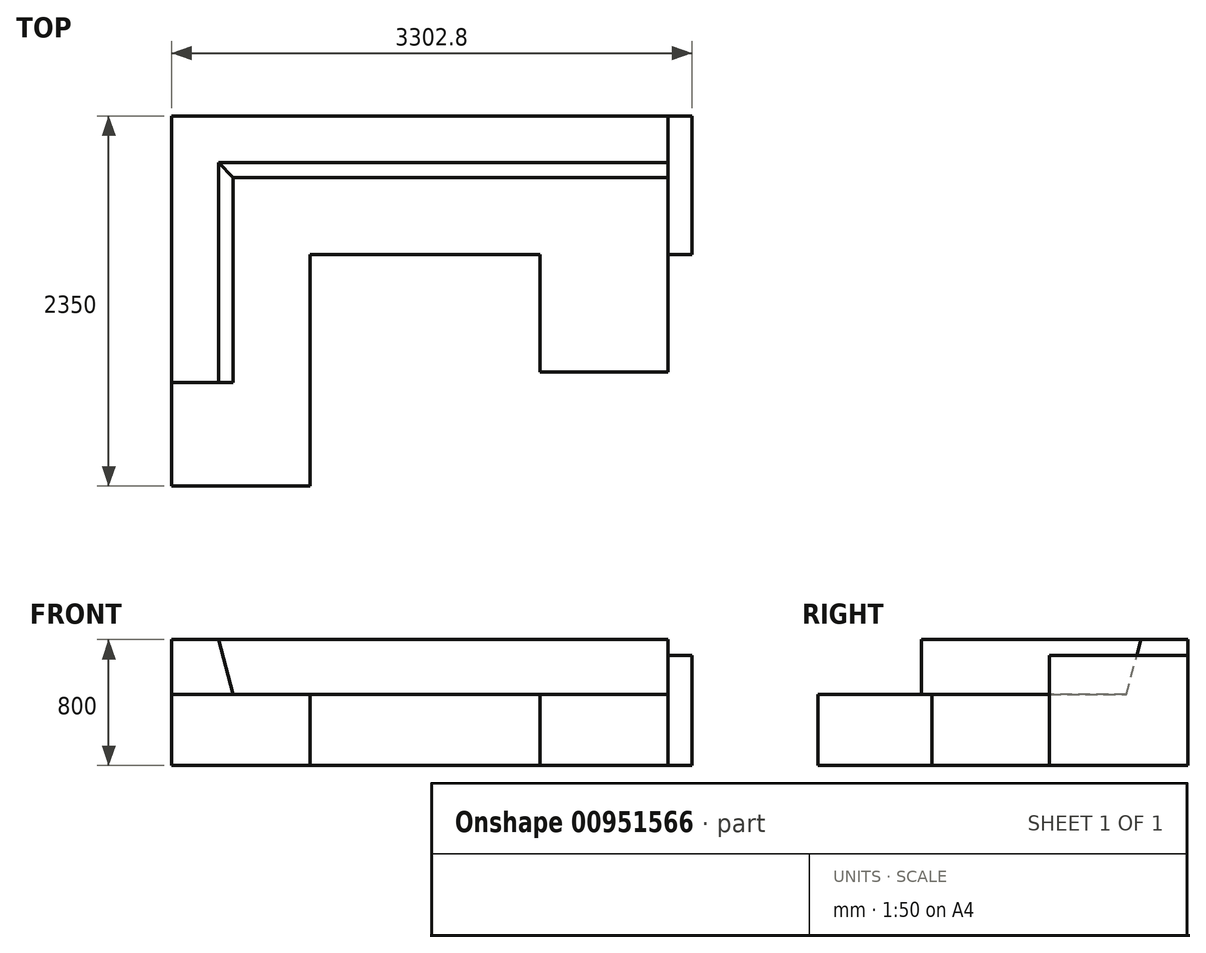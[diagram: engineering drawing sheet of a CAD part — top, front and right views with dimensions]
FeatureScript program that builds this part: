
annotation { "Feature Type Name" : "Feature", "Feature Type Description" : "" }
export const myFeature = defineFeature(function(context is Context, id is Id, definition is map)
    precondition{}
    {
        {
            var Q0;
            Q0=qCreatedBy(makeId("Top.planeOp"),FACE);
            var sketch = newSketch(context, id + "F0", { "sketchPlane" : qUnion([Q0])});
            skLineSegment(sketch, "E0", {"start": v(0, 0) * mm, "end": v(0, 2350) * mm});
            skLineSegment(sketch, "E1", {"start": v(0, 2350) * mm, "end": v(3302.8, 2350) * mm});
            skLineSegment(sketch, "E2", {"start": v(0, 0) * mm, "end": v(879.48, 0) * mm});
            skLineSegment(sketch, "E3", {"start": v(3302.8, 2350) * mm, "end": v(3302.8, 1470.52) * mm});
            skLineSegment(sketch, "E4", {"start": v(879.48, 0) * mm, "end": v(879.48, 1470.52) * mm});
            skLineSegment(sketch, "E5", {"start": v(879.48, 1470.52) * mm, "end": v(3302.8, 1470.52) * mm});
            skSolve(sketch);
        }
        {
            var Q0;
            Q0=qSketchRegion(id+"F0",true);
            extrude(context, id + "F1", {"entities" : qUnion([Q0]), "depth" : 450 * mm, "offsetDistance" : 25.4 * mm});
        }
        {
            var Q0;
            Q0=makeQuery(id+"F1.opExtrude","CAP_FACE",FACE,{"disambiguationData":[OSD([sQuery(id+"F0.wireOp",EDGE,"E0"),sQuery(id+"F0.wireOp",EDGE,"E1"),sQuery(id+"F0.wireOp",EDGE,"E2"),sQuery(id+"F0.wireOp",EDGE,"E3"),sQuery(id+"F0.wireOp",EDGE,"E4"),sQuery(id+"F0.wireOp",EDGE,"E5")])],"isStart":false});
            var sketch = newSketch(context, id + "F2", { "sketchPlane" : qUnion([Q0])});
            skLineSegment(sketch, "E6.bottom", {"start": v(879.48, 0) * mm, "end": v(0, 0) * mm});
            skLineSegment(sketch, "E6.top", {"start": v(879.48, 150) * mm, "end": v(0, 150) * mm});
            skLineSegment(sketch, "E6.left", {"start": v(879.48, 0) * mm, "end": v(879.48, 150) * mm});
            skLineSegment(sketch, "E6.right", {"start": v(0, 0) * mm, "end": v(0, 150) * mm});
            skLineSegment(sketch, "E7.bottom", {"start": v(3302.8, 1470.52) * mm, "end": v(3152.8, 1470.52) * mm});
            skLineSegment(sketch, "E7.top", {"start": v(3302.8, 2350) * mm, "end": v(3152.8, 2350) * mm});
            skLineSegment(sketch, "E7.left", {"start": v(3302.8, 1470.52) * mm, "end": v(3302.8, 2350) * mm});
            skLineSegment(sketch, "E7.right", {"start": v(3152.8, 1470.52) * mm, "end": v(3152.8, 2350) * mm});
            skSolve(sketch);
        }
        {
            var Q0;
            Q0=qSketchRegion(id+"F2",true);
            extrude(context, id + "F3", {"entities" : qUnion([Q0]), "operationType" : NewBodyOperationType.ADD, "depth" : 700 * mm - 450 * mm, "offsetDistance" : 25.4 * mm});
        }
        {
            var Q0;
            Q0=makeQuery(id+"F3.opExtrude","SWEPT_FACE",FACE,{"disambiguationData":[OSD([sQuery(id+"F2.wireOp",EDGE,"E6.top")])]});
            var sketch = newSketch(context, id + "F4", { "sketchPlane" : qUnion([Q0])});
            skLineSegment(sketch, "E8", {"start": v(0, 450) * mm, "end": v(0, 800) * mm});
            skLineSegment(sketch, "E9", {"start": v(0, 800) * mm, "end": v(-296.74, 800) * mm});
            skLineSegment(sketch, "E10", {"start": v(-296.74, 800) * mm, "end": v(-390.52, 450) * mm});
            skLineSegment(sketch, "E11", {"start": v(-390.52, 450) * mm, "end": v(0, 450) * mm});
            skSolve(sketch);
        }
        {
            var Q0;
            Q0=qSketchRegion(id+"F4",true);
            var Q1;
            Q1=makeQuery(id+"F3.boolean.opBoolean","MERGE",FACE,{"derivedFrom":[makeQuery(id+"F1.opExtrude","SWEPT_FACE",FACE,{"disambiguationData":[OSD([sQuery(id+"F0.wireOp",EDGE,"E1")])]}),makeQuery(id+"F3.opExtrude","SWEPT_FACE",FACE,{"disambiguationData":[OSD([sQuery(id+"F2.wireOp",EDGE,"E7.top")])]})]});
            extrude(context, id + "F5", {"entities" : qUnion([Q0]), "operationType" : NewBodyOperationType.ADD, "endBound" : BoundingType.UP_TO_SURFACE, "depth" : 25.4 * mm, "endBoundEntityFace" : qUnion([Q1]), "offsetDistance" : 25.4 * mm});
        }
        {
            var Q0;
            Q0=makeQuery(id+"F3.opExtrude","SWEPT_FACE",FACE,{"disambiguationData":[OSD([sQuery(id+"F2.wireOp",EDGE,"E7.right")])]});
            var sketch = newSketch(context, id + "F6", { "sketchPlane" : qUnion([Q0])});
            skLineSegment(sketch, "E12", {"start": v(-2350, 450) * mm, "end": v(-1959.47, 450) * mm});
            skLineSegment(sketch, "E13", {"start": v(-1959.47, 450) * mm, "end": v(-2053.26, 800) * mm});
            skLineSegment(sketch, "E14", {"start": v(-2053.26, 800) * mm, "end": v(-2350, 800) * mm});
            skLineSegment(sketch, "E15", {"start": v(-2350, 800) * mm, "end": v(-2350, 450) * mm});
            skSolve(sketch);
        }
        {
            var Q0;
            Q0=qSketchRegion(id+"F6",true);
            extrude(context, id + "F7", {"entities" : qUnion([Q0]), "operationType" : NewBodyOperationType.ADD, "endBound" : BoundingType.UP_TO_NEXT, "depth" : 25.4 * mm, "offsetDistance" : 25.4 * mm});
        }
        {
            var Q0;
            Q0=makeQuery(id+"F3.boolean.opBoolean","MERGE",FACE,{"derivedFrom":[makeQuery(id+"F1.opExtrude","SWEPT_FACE",FACE,{"disambiguationData":[OSD([sQuery(id+"F0.wireOp",EDGE,"E4")])]}),makeQuery(id+"F3.opExtrude","SWEPT_FACE",FACE,{"disambiguationData":[OSD([sQuery(id+"F2.wireOp",EDGE,"E6.left")])]})]});
            var sketch = newSketch(context, id + "F8", { "sketchPlane" : qUnion([Q0])});
            skLineSegment(sketch, "E16.bottom", {"start": v(658.57, 450) * mm, "end": v(0, 450) * mm});
            skLineSegment(sketch, "E16.top", {"start": v(658.57, 800) * mm, "end": v(0, 800) * mm});
            skLineSegment(sketch, "E16.left", {"start": v(658.57, 450) * mm, "end": v(658.57, 800) * mm});
            skLineSegment(sketch, "E16.right", {"start": v(0, 450) * mm, "end": v(0, 800) * mm});
            skSolve(sketch);
        }
        {
            var Q0;
            Q0=qSketchRegion(id+"F8",true);
            extrude(context, id + "F9", {"entities" : qUnion([Q0]), "operationType" : NewBodyOperationType.REMOVE, "endBound" : BoundingType.THROUGH_ALL, "oppositeDirection" : true, "depth" : 25.4 * mm, "offsetDistance" : 25.4 * mm});
        }
        {
            var Q0;
            Q0=makeQuery(id+"F9.boolean.opBoolean","MERGE",FACE,{"derivedFrom":[makeQuery(id+"F1.opExtrude","CAP_FACE",FACE,{"disambiguationData":[OSD([sQuery(id+"F0.wireOp",EDGE,"E0"),sQuery(id+"F0.wireOp",EDGE,"E1"),sQuery(id+"F0.wireOp",EDGE,"E2"),sQuery(id+"F0.wireOp",EDGE,"E3"),sQuery(id+"F0.wireOp",EDGE,"E4"),sQuery(id+"F0.wireOp",EDGE,"E5")])],"isStart":false})],"fromTools":[makeQuery(id+"F9.opExtrude","SWEPT_FACE",FACE,{"disambiguationData":[OSD([sQuery(id+"F8.wireOp",EDGE,"E16.bottom")])]})]});
            var sketch = newSketch(context, id + "F10", { "sketchPlane" : qUnion([Q0])});
            skLineSegment(sketch, "E17.bottom", {"start": v(3152.8, 1470.52) * mm, "end": v(2340, 1470.52) * mm});
            skLineSegment(sketch, "E17.top", {"start": v(3152.8, 724.4) * mm, "end": v(2340, 724.4) * mm});
            skLineSegment(sketch, "E17.left", {"start": v(3152.8, 1470.52) * mm, "end": v(3152.8, 724.4) * mm});
            skLineSegment(sketch, "E17.right", {"start": v(2340, 1470.52) * mm, "end": v(2340, 724.4) * mm});
            skSolve(sketch);
        }
        {
            var Q0;
            Q0 = qSketchRegion(id + "F10", true);
            var Q1;
            Q1=makeQuery(id+"F1.opExtrude","CAP_FACE",FACE,{"disambiguationData":[OSD([sQuery(id+"F0.wireOp",EDGE,"E0"),sQuery(id+"F0.wireOp",EDGE,"E1"),sQuery(id+"F0.wireOp",EDGE,"E2"),sQuery(id+"F0.wireOp",EDGE,"E3"),sQuery(id+"F0.wireOp",EDGE,"E4"),sQuery(id+"F0.wireOp",EDGE,"E5")])],"isStart":true});
            extrude(context, id + "F11", {"entities" : qUnion([Q0]), "operationType" : NewBodyOperationType.ADD, "endBound" : BoundingType.UP_TO_SURFACE, "oppositeDirection" : true, "depth" : 25.4 * mm, "endBoundEntityFace" : qUnion([Q1]), "offsetDistance" : 25.4 * mm});
        }
    });
